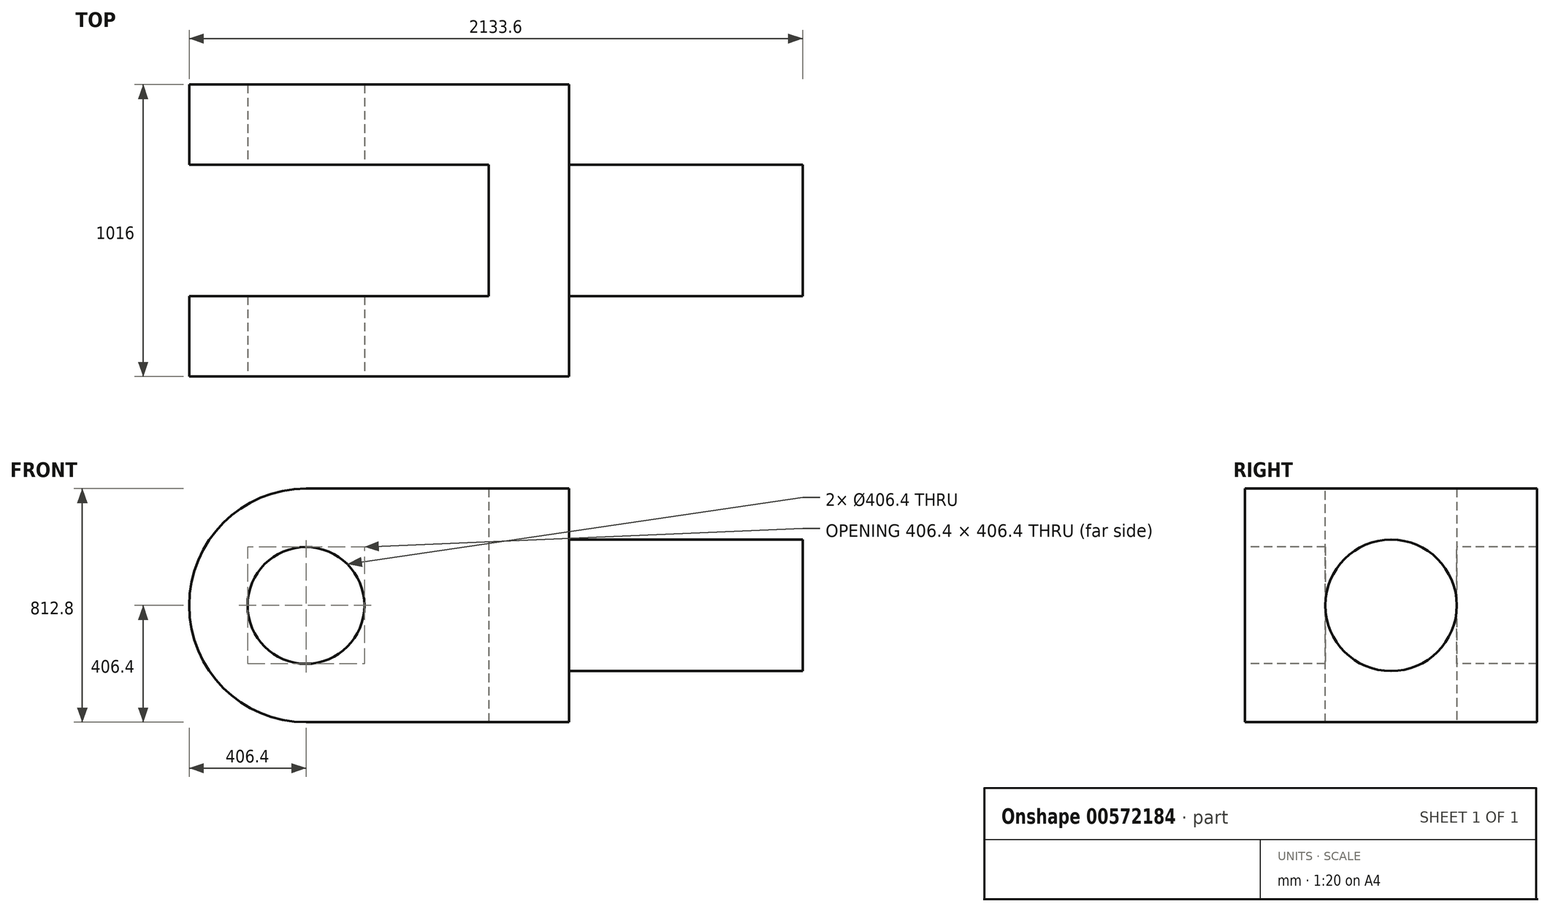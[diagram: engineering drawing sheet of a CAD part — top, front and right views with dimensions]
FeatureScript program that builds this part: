
annotation { "Feature Type Name" : "Feature", "Feature Type Description" : "" }
export const myFeature = defineFeature(function(context is Context, id is Id, definition is map)
    precondition{}
    {
        {
            var Q0;
            Q0=qCreatedBy(makeId("Top.planeOp"),FACE);
            var sketch = newSketch(context, id + "F0", { "sketchPlane" : qUnion([Q0])});
            skLineSegment(sketch, "E0", {"start": v(0, 0) * mm, "end": v(1320.8, 0) * mm});
            skLineSegment(sketch, "E1", {"start": v(0, 0) * mm, "end": v(0, 279.4) * mm});
            skLineSegment(sketch, "E2", {"start": v(0, 279.4) * mm, "end": v(1041.4, 279.4) * mm});
            skLineSegment(sketch, "E3", {"start": v(1041.4, 279.4) * mm, "end": v(1041.4, 736.6) * mm});
            skLineSegment(sketch, "E4", {"start": v(1041.4, 736.6) * mm, "end": v(0, 736.6) * mm});
            skLineSegment(sketch, "E5", {"start": v(0, 736.6) * mm, "end": v(0, 1016) * mm});
            skLineSegment(sketch, "E6", {"start": v(0, 1016) * mm, "end": v(1320.8, 1016) * mm});
            skLineSegment(sketch, "E7", {"start": v(1320.8, 1016) * mm, "end": v(1320.8, 0) * mm});
            skLineSegment(sketch, "E8", {"start": v(1320.8, 736.6) * mm, "end": v(2133.6, 736.6) * mm});
            skLineSegment(sketch, "E9", {"start": v(1320.8, 279.4) * mm, "end": v(2133.6, 279.4) * mm});
            skLineSegment(sketch, "E10", {"start": v(2133.6, 736.6) * mm, "end": v(2133.6, 279.4) * mm});
            skSolve(sketch);
        }
        {
            var Q0;
            Q0 = qSketchRegion(id + "F0", true);
            extrude(context, id + "F1", {"entities" : qUnion([Q0]), "depth" : 812.8 * mm, "offsetDistance" : 25.4 * mm});
        }
        {
            var Q0;
            Q0=makeQuery(id+"F1.opExtrude","SWEPT_FACE",FACE,{"disambiguationData":[OSD([sQuery(id+"F0.wireOp",EDGE,"E10")])]});
            var sketch = newSketch(context, id + "F2", { "sketchPlane" : qUnion([Q0])});
            skCircle(sketch, "E11", {"center": v(508, 406.4) * mm, "radius": 228.6 * mm});
            skSolve(sketch);
        }
        {
            var Q0;
            {var subQ1=sQuery(id+"F0.wireOp",EDGE,"E10");var subQ6=makeQuery(id+"F1.opExtrude","CAP_EDGE",EDGE,{"disambiguationData":[OSD([subQ1])],"isStart":false});Q0=makeQuery(id+"F2.imprint","IMPRINT",FACE,{"disambiguationData":[TD([[makeQuery(id+"F2.imprint","IMPRINT",EDGE,{"derivedFrom":subQ6}),1.0]])]});}
            var Q1;
            {var subQ1=sQuery(id+"F0.wireOp",EDGE,"E10");var subQ6=makeQuery(id+"F1.opExtrude","CAP_EDGE",EDGE,{"disambiguationData":[OSD([subQ1])],"isStart":true});Q1=makeQuery(id+"F2.imprint","IMPRINT",FACE,{"disambiguationData":[TD([[makeQuery(id+"F2.imprint","IMPRINT",EDGE,{"derivedFrom":subQ6}),-1.0]])]});}
            extrude(context, id + "F3", {"entities" : qUnion([Q0, Q1]), "operationType" : NewBodyOperationType.REMOVE, "oppositeDirection" : true, "depth" : 812.8 * mm, "offsetDistance" : 25.4 * mm});
        }
        {
            var Q0;
            Q0=makeQuery(id+"F1.opExtrude","SWEPT_FACE",FACE,{"disambiguationData":[OSD([sQuery(id+"F0.wireOp",EDGE,"E0")])]});
            var sketch = newSketch(context, id + "F4", { "sketchPlane" : qUnion([Q0])});
            skCircle(sketch, "E12", {"center": v(406.4, 406.4) * mm, "radius": 203.2 * mm});
            skSolve(sketch);
        }
        {
            var Q0;
            Q0=makeQuery(id+"F4.imprint","IMPRINT",FACE,{"disambiguationData":[TD([[makeQuery(id+"F4.imprint","IMPRINT",EDGE,{"derivedFrom":sQuery(id+"F4.wireOp",EDGE,"E12")}),1.0]])]});
            extrude(context, id + "F5", {"entities" : qUnion([Q0]), "operationType" : NewBodyOperationType.REMOVE, "endBound" : BoundingType.THROUGH_ALL, "oppositeDirection" : true, "depth" : 25.4 * mm, "offsetDistance" : 25.4 * mm});
        }
        {
            var Q0;
            Q0=makeQuery(id+"F1.opExtrude","CAP_EDGE",EDGE,{"disambiguationData":[OSD([sQuery(id+"F0.wireOp",EDGE,"E5")])],"isStart":false});
            fillet(context, id + "F6", {"entities" : qUnion([Q0]), "radius" : 406.4 * mm, "tangentPropagation" : true, "allowEdgeOverflow" : false});
        }
        {
            var Q0;
            Q0=makeQuery(id+"F1.opExtrude","CAP_EDGE",EDGE,{"disambiguationData":[OSD([sQuery(id+"F0.wireOp",EDGE,"E5")])],"isStart":true});
            fillet(context, id + "F7", {"entities" : qUnion([Q0]), "radius" : 406.4 * mm, "tangentPropagation" : true, "allowEdgeOverflow" : false});
        }
        {
            var Q0;
            Q0=makeQuery(id+"F1.opExtrude","CAP_EDGE",EDGE,{"disambiguationData":[OSD([sQuery(id+"F0.wireOp",EDGE,"E1")])],"isStart":true});
            fillet(context, id + "F8", {"entities" : qUnion([Q0]), "radius" : 406.4 * mm, "tangentPropagation" : true, "allowEdgeOverflow" : false});
        }
        {
            var Q0;
            Q0=makeQuery(id+"F1.opExtrude","CAP_EDGE",EDGE,{"disambiguationData":[OSD([sQuery(id+"F0.wireOp",EDGE,"E1")])],"isStart":false});
            fillet(context, id + "F9", {"entities" : qUnion([Q0]), "radius" : 406.4 * mm, "tangentPropagation" : true, "allowEdgeOverflow" : false});
        }
    });
